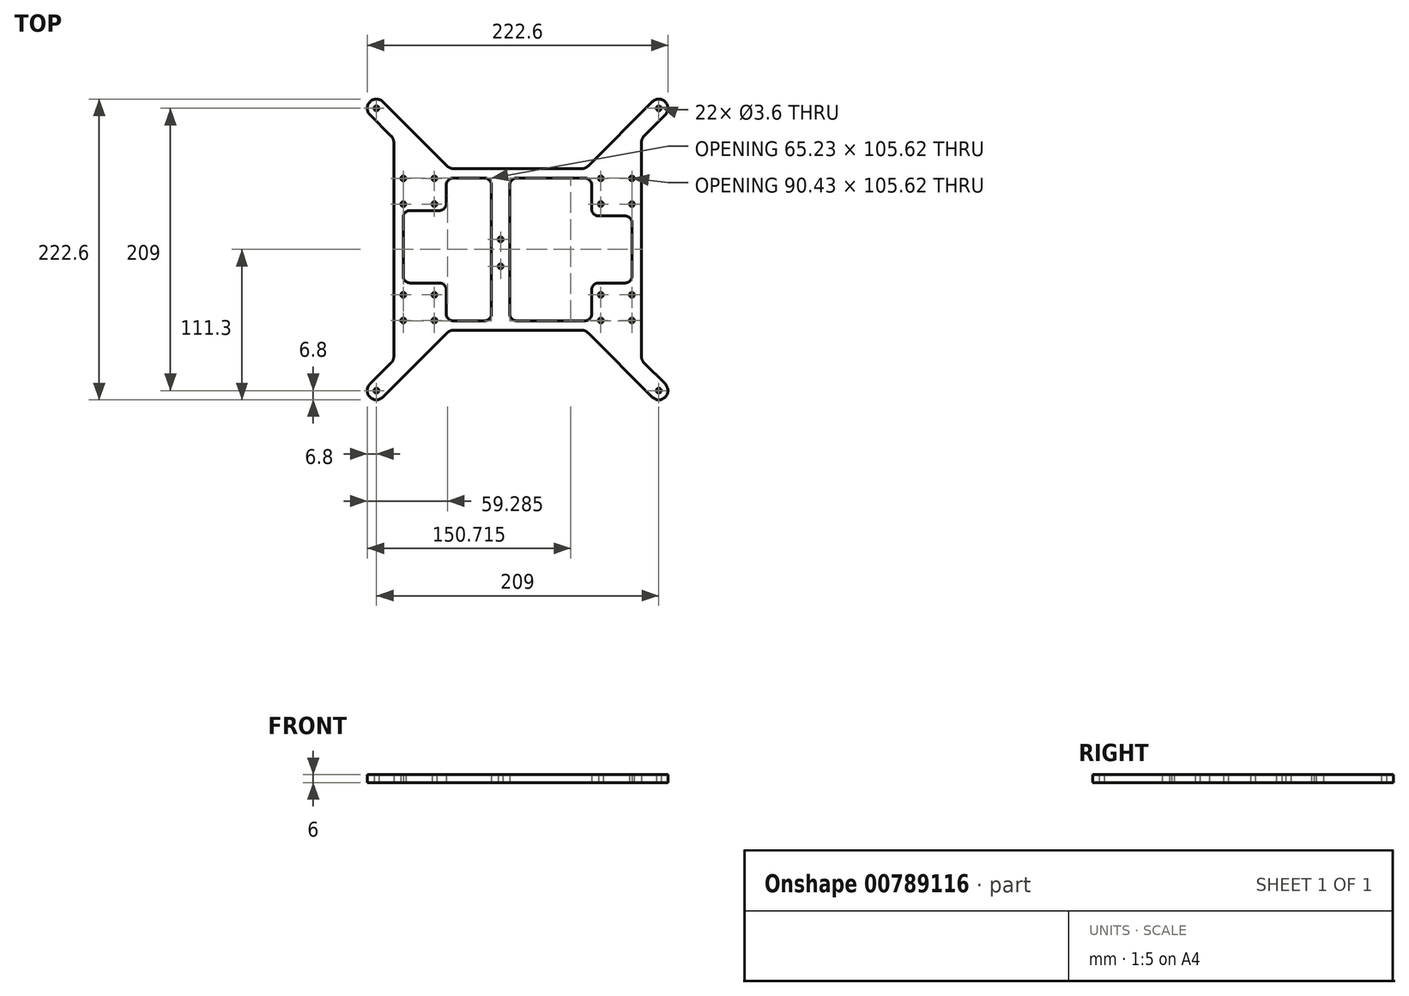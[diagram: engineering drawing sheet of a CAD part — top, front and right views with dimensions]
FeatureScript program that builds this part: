
annotation { "Feature Type Name" : "Feature", "Feature Type Description" : "" }
export const myFeature = defineFeature(function(context is Context, id is Id, definition is map)
    precondition{}
    {
        {
            var Q0;
            Q0=qCreatedBy(makeId("Top.planeOp"),FACE);
            var sketch = newSketch(context, id + "F0", { "sketchPlane" : qUnion([Q0])});
            skLineSegment(sketch, "E0.bottom", {"start": v(107.6, 107.6) * mm, "end": v(-107.6, 107.6) * mm});
            skLineSegment(sketch, "E0.top", {"start": v(107.6, -107.6) * mm, "end": v(-107.6, -107.6) * mm});
            skLineSegment(sketch, "E0.left", {"start": v(107.6, 107.6) * mm, "end": v(107.6, -107.6) * mm});
            skLineSegment(sketch, "E0.right", {"start": v(-107.6, 107.6) * mm, "end": v(-107.6, -107.6) * mm});
            skPoint(sketch, "E0.middle", {"position": v(0, 0) * mm});
            skLineSegment(sketch, "E1.bottom", {"start": v(104.5, 104.5) * mm, "end": v(-104.5, 104.5) * mm, "construction": true});
            skLineSegment(sketch, "E1.top", {"start": v(104.5, -104.5) * mm, "end": v(-104.5, -104.5) * mm, "construction": true});
            skLineSegment(sketch, "E1.left", {"start": v(104.5, 104.5) * mm, "end": v(104.5, -104.5) * mm, "construction": true});
            skLineSegment(sketch, "E1.right", {"start": v(-104.5, 104.5) * mm, "end": v(-104.5, -104.5) * mm, "construction": true});
            skCircle(sketch, "E2", {"center": v(104.5, 104.5) * mm, "radius": 1.8 * mm});
            skCircle(sketch, "E3", {"center": v(-104.5, 104.5) * mm, "radius": 1.8 * mm});
            skCircle(sketch, "E4", {"center": v(-104.5, -104.5) * mm, "radius": 1.8 * mm});
            skCircle(sketch, "E5", {"center": v(104.5, -104.5) * mm, "radius": 1.8 * mm});
            skCircle(sketch, "E6", {"center": v(-84.6, 52.6) * mm, "radius": 1.8 * mm});
            skCircle(sketch, "E7", {"center": v(-61.6, 52.6) * mm, "radius": 1.8 * mm});
            skCircle(sketch, "E8", {"center": v(-61.6, 33.6) * mm, "radius": 1.8 * mm});
            skCircle(sketch, "E9", {"center": v(-84.6, 33.6) * mm, "radius": 1.8 * mm});
            skCircle(sketch, "E10", {"center": v(61.6, 52.6) * mm, "radius": 1.8 * mm});
            skCircle(sketch, "E11", {"center": v(84.6, 52.6) * mm, "radius": 1.8 * mm});
            skCircle(sketch, "E12", {"center": v(84.6, 33.6) * mm, "radius": 1.8 * mm});
            skCircle(sketch, "E13", {"center": v(61.6, 33.6) * mm, "radius": 1.8 * mm});
            skCircle(sketch, "E14", {"center": v(61.6, -33.6) * mm, "radius": 1.8 * mm});
            skCircle(sketch, "E15", {"center": v(84.6, -33.6) * mm, "radius": 1.8 * mm});
            skCircle(sketch, "E16", {"center": v(84.6, -52.6) * mm, "radius": 1.8 * mm});
            skCircle(sketch, "E17", {"center": v(61.6, -52.6) * mm, "radius": 1.8 * mm});
            skCircle(sketch, "E18", {"center": v(-84.6, -33.6) * mm, "radius": 1.8 * mm});
            skCircle(sketch, "E19", {"center": v(-61.6, -33.6) * mm, "radius": 1.8 * mm});
            skCircle(sketch, "E20", {"center": v(-61.6, -52.6) * mm, "radius": 1.8 * mm});
            skCircle(sketch, "E21", {"center": v(-84.6, -52.6) * mm, "radius": 1.8 * mm});
            skLineSegment(sketch, "E22", {"start": v(-104.5, -104.5) * mm, "end": v(-99.7, -109.3) * mm, "construction": true});
            skLineSegment(sketch, "E23", {"start": v(-109.3, -99.7) * mm, "end": v(-104.5, -104.5) * mm, "construction": true});
            skLineSegment(sketch, "E24", {"start": v(99.7, -109.3) * mm, "end": v(104.5, -104.5) * mm, "construction": true});
            skLineSegment(sketch, "E25", {"start": v(109.3, -99.7) * mm, "end": v(104.5, -104.5) * mm, "construction": true});
            skLineSegment(sketch, "E26", {"start": v(99.7, 109.3) * mm, "end": v(104.5, 104.5) * mm, "construction": true});
            skLineSegment(sketch, "E27", {"start": v(109.3, 99.7) * mm, "end": v(104.5, 104.5) * mm, "construction": true});
            skLineSegment(sketch, "E28", {"start": v(-99.7, 109.3) * mm, "end": v(-104.5, 104.5) * mm, "construction": true});
            skLineSegment(sketch, "E29", {"start": v(-109.3, 99.7) * mm, "end": v(-104.5, 104.5) * mm, "construction": true});
            skLineSegment(sketch, "E30", {"start": v(-99.7, -109.3) * mm, "end": v(-52.24, -61.86) * mm});
            skLineSegment(sketch, "E31", {"start": v(99.7, -109.3) * mm, "end": v(52.24, -61.86) * mm});
            skLineSegment(sketch, "E32", {"start": v(-47.3, -59.81) * mm, "end": v(47.3, -59.81) * mm});
            skLineSegment(sketch, "E33", {"start": v(109.3, -99.7) * mm, "end": v(93.68, -84.06) * mm});
            skLineSegment(sketch, "E34", {"start": v(109.3, 99.7) * mm, "end": v(93.68, 84.06) * mm});
            skLineSegment(sketch, "E35", {"start": v(91.63, 79.11) * mm, "end": v(91.63, -79.11) * mm});
            skLineSegment(sketch, "E36", {"start": v(99.7, 109.3) * mm, "end": v(52.24, 61.86) * mm});
            skLineSegment(sketch, "E37", {"start": v(-99.7, 109.3) * mm, "end": v(-52.24, 61.86) * mm});
            skLineSegment(sketch, "E38", {"start": v(-47.3, 59.81) * mm, "end": v(47.3, 59.81) * mm});
            skLineSegment(sketch, "E39", {"start": v(-109.3, 99.7) * mm, "end": v(-93.68, 84.06) * mm});
            skLineSegment(sketch, "E40", {"start": v(-109.3, -99.7) * mm, "end": v(-93.68, -84.06) * mm});
            skLineSegment(sketch, "E41", {"start": v(-91.63, 79.11) * mm, "end": v(-91.63, -79.11) * mm});
            skCircle(sketch, "E42", {"center": v(-12.6, 7.5) * mm, "radius": 1.8 * mm});
            skCircle(sketch, "E43", {"center": v(-12.6, -12.5) * mm, "radius": 1.8 * mm});
            skArc(sketch, "E44", {"start": v(109.3, 99.7) * mm, "mid": v(109.3, 109.3) * mm, "end": v(99.7, 109.3) * mm});
            skArc(sketch, "E45", {"start": v(99.7, -109.3) * mm, "mid": v(109.3, -109.3) * mm, "end": v(109.3, -99.7) * mm});
            skArc(sketch, "E46", {"start": v(-109.3, -99.7) * mm, "mid": v(-109.3, -109.3) * mm, "end": v(-99.7, -109.3) * mm});
            skArc(sketch, "E47", {"start": v(-99.7, 109.3) * mm, "mid": v(-109.3, 109.3) * mm, "end": v(-109.3, 99.7) * mm});
            skPoint(sketch, "E48.visualSharp", {"position": v(-91.63, 82.01) * mm});
            skArc(sketch, "E48.filletArc", {"start": v(-91.63, 79.11) * mm, "mid": v(-92.16, 81.8) * mm, "end": v(-93.68, 84.06) * mm});
            skPoint(sketch, "E49.visualSharp", {"position": v(-50.2, 59.81) * mm});
            skArc(sketch, "E49.filletArc", {"start": v(-52.24, 61.86) * mm, "mid": v(-49.97, 60.34) * mm, "end": v(-47.3, 59.81) * mm});
            skPoint(sketch, "E50.visualSharp", {"position": v(50.2, 59.81) * mm});
            skArc(sketch, "E50.filletArc", {"start": v(47.3, 59.81) * mm, "mid": v(49.97, 60.34) * mm, "end": v(52.24, 61.86) * mm});
            skPoint(sketch, "E51.visualSharp", {"position": v(91.63, 82.01) * mm});
            skArc(sketch, "E51.filletArc", {"start": v(93.68, 84.06) * mm, "mid": v(92.16, 81.8) * mm, "end": v(91.63, 79.11) * mm});
            skPoint(sketch, "E52.visualSharp", {"position": v(91.63, -82.01) * mm});
            skArc(sketch, "E52.filletArc", {"start": v(91.63, -79.11) * mm, "mid": v(92.16, -81.8) * mm, "end": v(93.68, -84.06) * mm});
            skPoint(sketch, "E53.visualSharp", {"position": v(-50.2, -59.81) * mm});
            skArc(sketch, "E53.filletArc", {"start": v(-47.3, -59.81) * mm, "mid": v(-49.97, -60.34) * mm, "end": v(-52.24, -61.86) * mm});
            skPoint(sketch, "E54.visualSharp", {"position": v(50.2, -59.81) * mm});
            skArc(sketch, "E54.filletArc", {"start": v(52.24, -61.86) * mm, "mid": v(49.97, -60.34) * mm, "end": v(47.3, -59.81) * mm});
            skPoint(sketch, "E55.visualSharp", {"position": v(-91.63, -82.01) * mm});
            skArc(sketch, "E55.filletArc", {"start": v(-93.68, -84.06) * mm, "mid": v(-92.16, -81.8) * mm, "end": v(-91.63, -79.11) * mm});
            skLineSegment(sketch, "E56", {"start": v(-12.6, -10.5) * mm, "end": v(-19.4, -10.5) * mm, "construction": true});
            skLineSegment(sketch, "E57", {"start": v(-12.6, 7.5) * mm, "end": v(-5.8, 7.5) * mm, "construction": true});
            skLineSegment(sketch, "E58.bottom", {"start": v(-0.8, 52.81) * mm, "end": v(49.8, 52.81) * mm});
            skLineSegment(sketch, "E58.top", {"start": v(-0.8, -52.81) * mm, "end": v(49.8, -52.81) * mm});
            skLineSegment(sketch, "E58.left", {"start": v(-5.8, 47.81) * mm, "end": v(-5.8, -47.81) * mm});
            skLineSegment(sketch, "E59.top", {"start": v(-24.4, -52.81) * mm, "end": v(-47.8, -52.81) * mm});
            skLineSegment(sketch, "E59.left", {"start": v(-19.4, 47.81) * mm, "end": v(-19.4, -47.81) * mm});
            skLineSegment(sketch, "E60.bottom", {"start": v(59.8, 24.8) * mm, "end": v(79.63, 24.8) * mm});
            skLineSegment(sketch, "E60.top", {"start": v(59.8, -24.8) * mm, "end": v(79.63, -24.8) * mm});
            skLineSegment(sketch, "E60.right", {"start": v(84.63, 19.8) * mm, "end": v(84.63, -19.8) * mm});
            skLineSegment(sketch, "E61.bottom", {"start": v(-57.8, 28.8) * mm, "end": v(-79.63, 28.8) * mm});
            skLineSegment(sketch, "E61.top", {"start": v(-57.8, -24.8) * mm, "end": v(-79.63, -24.8) * mm});
            skLineSegment(sketch, "E61.right", {"start": v(-84.63, 23.8) * mm, "end": v(-84.63, -19.8) * mm});
            skPoint(sketch, "E62.visualSharp", {"position": v(-19.4, 52.81) * mm});
            skArc(sketch, "E62.filletArc", {"start": v(-19.4, 47.81) * mm, "mid": v(-20.86, 51.35) * mm, "end": v(-24.4, 52.81) * mm});
            skPoint(sketch, "E63.visualSharp", {"position": v(-52.8, 52.81) * mm});
            skLineSegment(sketch, "E64", {"start": v(-52.8, -29.8) * mm, "end": v(-52.8, -47.81) * mm});
            skLineSegment(sketch, "E65", {"start": v(54.8, 29.8) * mm, "end": v(54.8, 47.81) * mm});
            skLineSegment(sketch, "E66", {"start": v(54.8, -29.8) * mm, "end": v(54.8, -47.81) * mm});
            skPoint(sketch, "E67.visualSharp", {"position": v(-52.8, 28.8) * mm});
            skArc(sketch, "E67.filletArc", {"start": v(-57.8, 28.8) * mm, "mid": v(-54.26, 30.26) * mm, "end": v(-52.8, 33.8) * mm});
            skPoint(sketch, "E68.visualSharp", {"position": v(-84.63, 28.8) * mm});
            skArc(sketch, "E68.filletArc", {"start": v(-79.63, 28.8) * mm, "mid": v(-83.17, 27.34) * mm, "end": v(-84.63, 23.8) * mm});
            skPoint(sketch, "E69.visualSharp", {"position": v(-84.63, -24.8) * mm});
            skArc(sketch, "E69.filletArc", {"start": v(-84.63, -19.8) * mm, "mid": v(-83.17, -23.34) * mm, "end": v(-79.63, -24.8) * mm});
            skPoint(sketch, "E70.visualSharp", {"position": v(-52.8, -24.8) * mm});
            skArc(sketch, "E70.filletArc", {"start": v(-52.8, -29.8) * mm, "mid": v(-54.26, -26.26) * mm, "end": v(-57.8, -24.8) * mm});
            skPoint(sketch, "E71.visualSharp", {"position": v(-52.8, -52.81) * mm});
            skArc(sketch, "E71.filletArc", {"start": v(-52.8, -47.81) * mm, "mid": v(-51.34, -51.35) * mm, "end": v(-47.8, -52.81) * mm});
            skPoint(sketch, "E72.visualSharp", {"position": v(-19.4, -52.81) * mm});
            skArc(sketch, "E72.filletArc", {"start": v(-24.4, -52.81) * mm, "mid": v(-20.86, -51.35) * mm, "end": v(-19.4, -47.81) * mm});
            skPoint(sketch, "E73.visualSharp", {"position": v(-5.8, -52.81) * mm});
            skArc(sketch, "E73.filletArc", {"start": v(-5.8, -47.81) * mm, "mid": v(-4.34, -51.35) * mm, "end": v(-0.8, -52.81) * mm});
            skPoint(sketch, "E74.visualSharp", {"position": v(54.8, -52.81) * mm});
            skArc(sketch, "E74.filletArc", {"start": v(49.8, -52.81) * mm, "mid": v(53.34, -51.35) * mm, "end": v(54.8, -47.81) * mm});
            skPoint(sketch, "E75.visualSharp", {"position": v(54.8, -24.8) * mm});
            skArc(sketch, "E75.filletArc", {"start": v(59.8, -24.8) * mm, "mid": v(56.26, -26.26) * mm, "end": v(54.8, -29.8) * mm});
            skPoint(sketch, "E76.visualSharp", {"position": v(84.63, -24.8) * mm});
            skArc(sketch, "E76.filletArc", {"start": v(79.63, -24.8) * mm, "mid": v(83.17, -23.33) * mm, "end": v(84.63, -19.8) * mm});
            skPoint(sketch, "E77.visualSharp", {"position": v(84.63, 24.8) * mm});
            skArc(sketch, "E77.filletArc", {"start": v(84.63, 19.8) * mm, "mid": v(83.17, 23.34) * mm, "end": v(79.63, 24.8) * mm});
            skPoint(sketch, "E78.visualSharp", {"position": v(54.8, 24.8) * mm});
            skArc(sketch, "E78.filletArc", {"start": v(54.8, 29.8) * mm, "mid": v(56.26, 26.26) * mm, "end": v(59.8, 24.8) * mm});
            skPoint(sketch, "E79.visualSharp", {"position": v(54.8, 52.81) * mm});
            skArc(sketch, "E79.filletArc", {"start": v(54.8, 47.81) * mm, "mid": v(53.34, 51.35) * mm, "end": v(49.8, 52.81) * mm});
            skPoint(sketch, "E80.visualSharp", {"position": v(-5.8, 52.81) * mm});
            skArc(sketch, "E80.filletArc", {"start": v(-0.8, 52.81) * mm, "mid": v(-4.34, 51.35) * mm, "end": v(-5.8, 47.81) * mm});
            skLineSegment(sketch, "E81", {"start": v(-52.8, 33.8) * mm, "end": v(-52.8, 47.81) * mm});
            skLineSegment(sketch, "E82", {"start": v(-47.8, 52.81) * mm, "end": v(-24.4, 52.81) * mm});
            skArc(sketch, "E83.filletArc", {"start": v(-47.8, 52.81) * mm, "mid": v(-51.34, 51.35) * mm, "end": v(-52.8, 47.81) * mm});
            skSolve(sketch);
        }
        {
            var Q0;
            Q0=makeQuery(id+"F0.imprint","IMPRINT",FACE,{"disambiguationData":[TD([[makeQuery(id+"F0.imprint","IMPRINT",EDGE,{"derivedFrom":sQuery(id+"F0.wireOp",EDGE,"E2")}),-1.0]])]});
            var Q1;
            {var subQ0=sQuery(id+"F0.wireOp",EDGE,"E47");Q1=makeQuery(id+"F0.imprint","IMPRINT",FACE,{"disambiguationData":[TD([[makeQuery(id+"F0.imprint","IMPRINT",EDGE,{"derivedFrom":subQ0}),1.0]])]});}
            var Q2;
            {var subQ0=sQuery(id+"F0.wireOp",EDGE,"E44");Q2=makeQuery(id+"F0.imprint","IMPRINT",FACE,{"disambiguationData":[TD([[makeQuery(id+"F0.imprint","IMPRINT",EDGE,{"derivedFrom":subQ0}),1.0]])]});}
            var Q3;
            {var subQ0=sQuery(id+"F0.wireOp",EDGE,"E45");Q3=makeQuery(id+"F0.imprint","IMPRINT",FACE,{"disambiguationData":[TD([[makeQuery(id+"F0.imprint","IMPRINT",EDGE,{"derivedFrom":subQ0}),1.0]])]});}
            var Q4;
            {var subQ0=sQuery(id+"F0.wireOp",EDGE,"E46");Q4=makeQuery(id+"F0.imprint","IMPRINT",FACE,{"disambiguationData":[TD([[makeQuery(id+"F0.imprint","IMPRINT",EDGE,{"derivedFrom":subQ0}),1.0]])]});}
            var Q5;
            Q5=makeQuery(id+"F0.imprint","IMPRINT",FACE,{"disambiguationData":[TD([[makeQuery(id+"F0.imprint","IMPRINT",EDGE,{"derivedFrom":sQuery(id+"F0.wireOp",EDGE,"E42")}),-1.0]])]});
            extrude(context, id + "F1", {"entities" : qUnion([Q0, Q1, Q2, Q3, Q4, Q5]), "depth" : 6 * mm, "offsetDistance" : 25 * mm});
        }
    });
